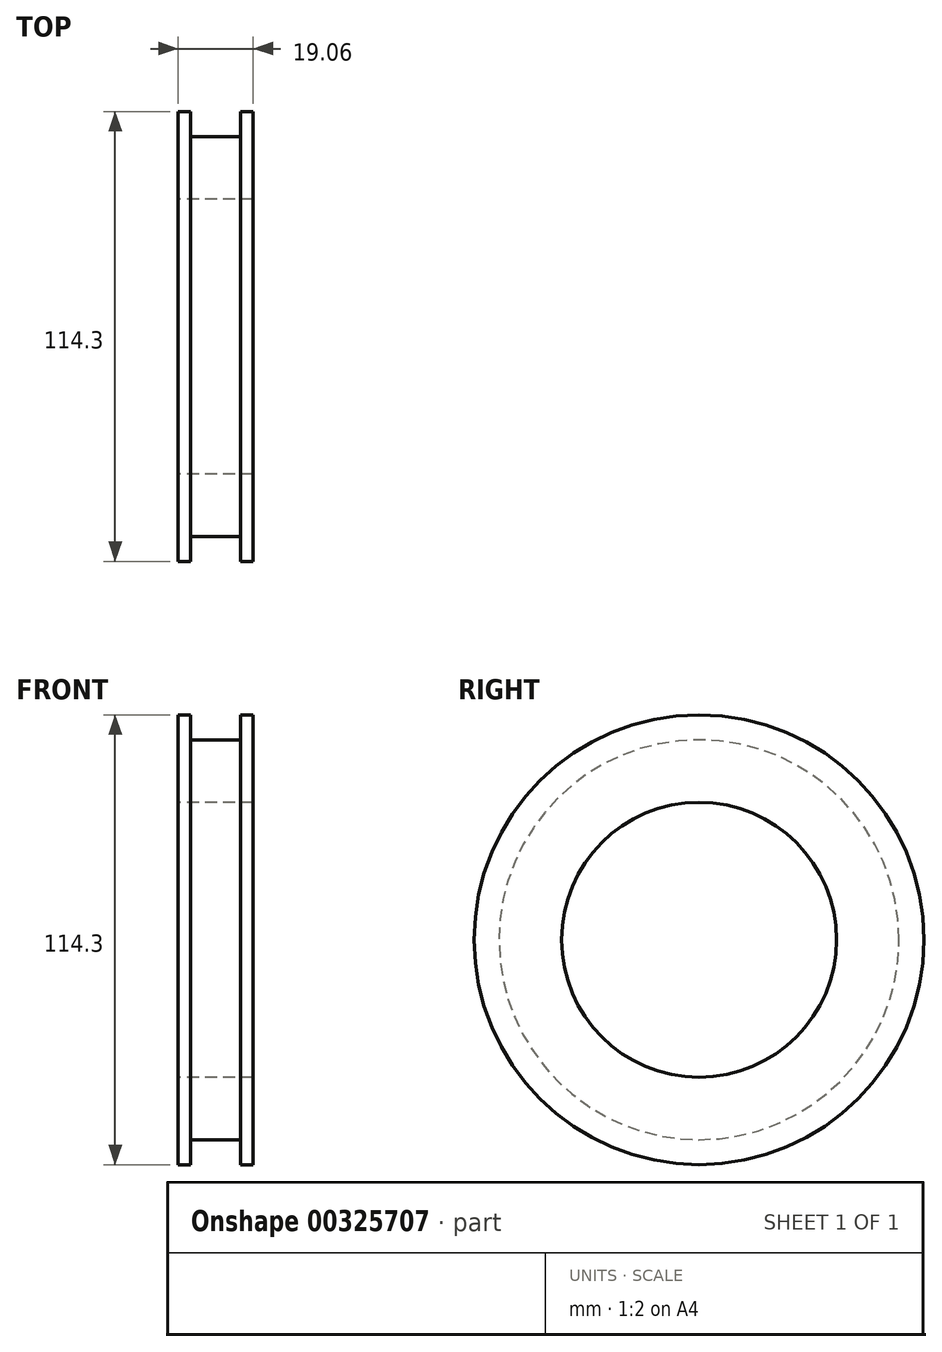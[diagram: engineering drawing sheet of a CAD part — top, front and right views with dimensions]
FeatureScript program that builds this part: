
annotation { "Feature Type Name" : "Feature", "Feature Type Description" : "" }
export const myFeature = defineFeature(function(context is Context, id is Id, definition is map)
    precondition{}
    {
        {
            var Q0;
            Q0=qCreatedBy(makeId("Right.planeOp"),FACE);
            var sketch = newSketch(context, id + "F0", { "sketchPlane" : qUnion([Q0])});
            skCircle(sketch, "E0", {"center": v(0, 0) * mm, "radius": 50.8 * mm});
            skCircle(sketch, "E1", {"center": v(0, 0) * mm, "radius": 34.93 * mm});
            skSolve(sketch);
        }
        {
            var Q0;
            Q0=qSketchRegion(id+"F0",true);
            extrude(context, id + "F1", {"entities" : qUnion([Q0]), "endBound" : BoundingType.SYMMETRIC, "depth" : 12.7 * mm});
        }
        {
            var Q0;
            Q0=makeQuery(id+"F1.opExtrude","CAP_FACE",FACE,{"disambiguationData":[OSD([sQuery(id+"F0.wireOp",EDGE,"E0"),sQuery(id+"F0.wireOp",EDGE,"E1")])],"isStart":false});
            var sketch = newSketch(context, id + "F2", { "sketchPlane" : qUnion([Q0])});
            skCircle(sketch, "E2.0", {"center": v(0, 0) * mm, "radius": 34.93 * mm});
            skCircle(sketch, "E3", {"center": v(0, 0) * mm, "radius": 57.15 * mm});
            skSolve(sketch);
        }
        {
            var Q0;
            Q0=qSketchRegion(id+"F2",true);
            extrude(context, id + "F3", {"entities" : qUnion([Q0]), "depth" : 3.17 * mm});
        }
        {
            var Q0;
            Q0=makeQuery(id+"F3.opExtrude","SWEPT_BODY",BODY,{"disambiguationData":[OSD([sQuery(id+"F2.wireOp",EDGE,"E2.0"),sQuery(id+"F2.wireOp",EDGE,"E3")])]});
            var Q1;
            Q1=qCreatedBy(makeId("Right.planeOp"),FACE);
            mirror(context, id + "F4", {"operationType" : NewBodyOperationType.ADD, "entities" : qUnion([Q0]), "mirrorPlane" : qUnion([Q1])});
        }
    });
